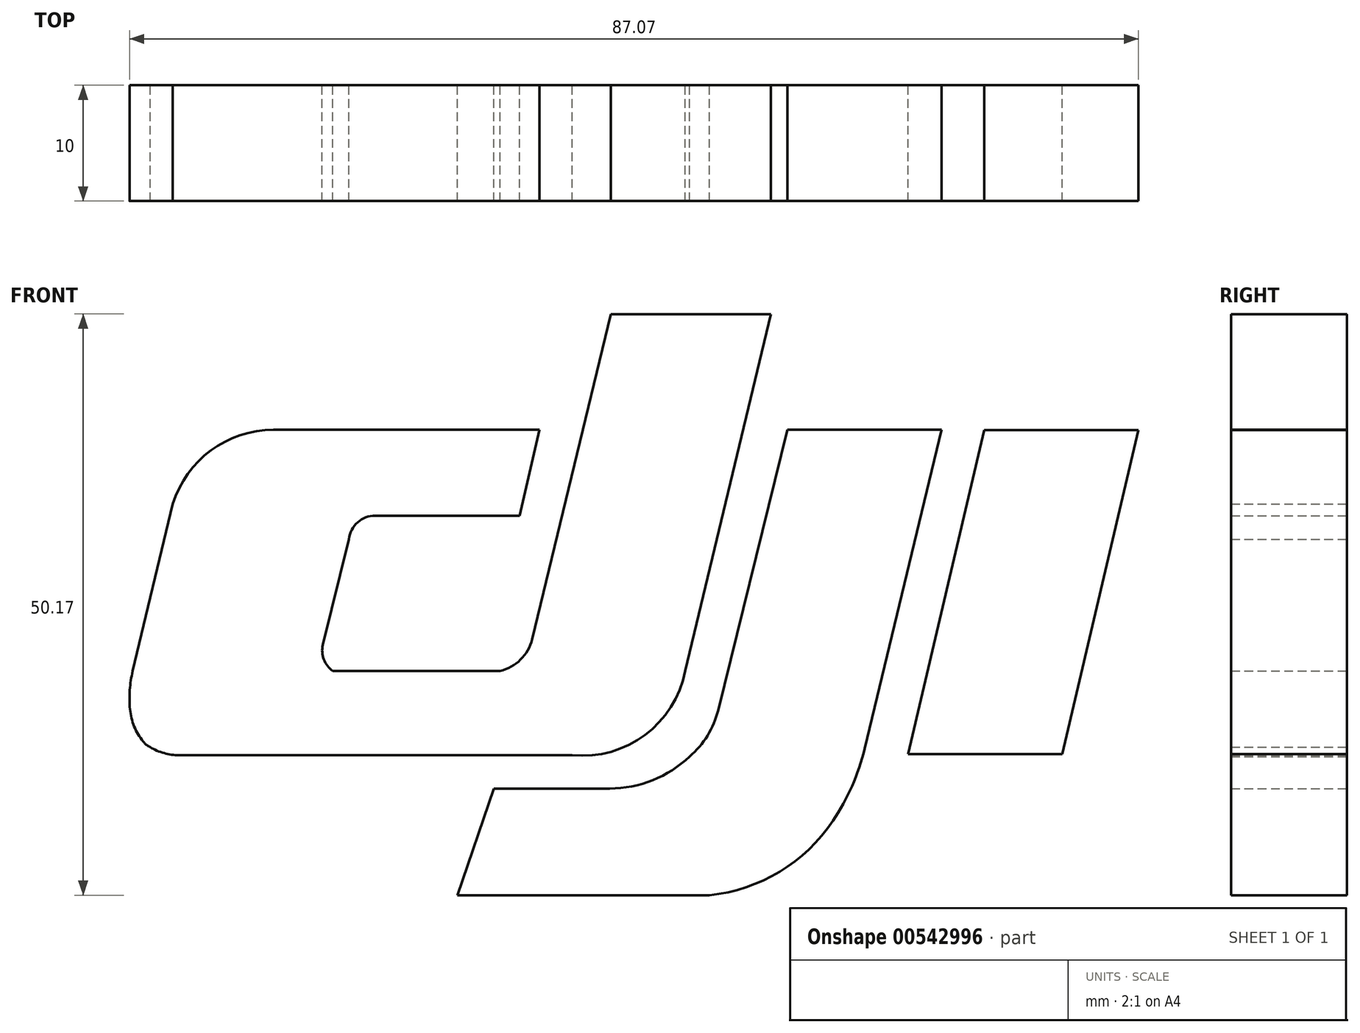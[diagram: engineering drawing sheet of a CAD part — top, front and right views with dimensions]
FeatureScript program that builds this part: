
annotation { "Feature Type Name" : "Feature", "Feature Type Description" : "" }
export const myFeature = defineFeature(function(context is Context, id is Id, definition is map)
    precondition{}
    {
        {
            var Q0;
            Q0=qCreatedBy(makeId("Front.planeOp"),FACE);
            var sketch = newSketch(context, id + "F0", { "sketchPlane" : qUnion([Q0])});
            skLineSegment(sketch, "E0", {"start": v(11.76, 25.1) * mm, "end": v(-2.04, 25.1) * mm});
            skLineSegment(sketch, "E1", {"start": v(-2.04, 25.1) * mm, "end": v(-8.84, -2.97) * mm});
            skLineSegment(sketch, "E2", {"start": v(11.76, 25.1) * mm, "end": v(4.38, -5.7) * mm});
            skLineSegment(sketch, "E3", {"start": v(-8.2, 15.11) * mm, "end": v(-9.92, 7.7) * mm});
            skLineSegment(sketch, "E4", {"start": v(-9.92, 7.7) * mm, "end": v(-22.36, 7.7) * mm});
            skLineSegment(sketch, "E5", {"start": v(-8.2, 15.11) * mm, "end": v(-31.15, 15.11) * mm});
            skLineSegment(sketch, "E6", {"start": v(-39.84, 8.7) * mm, "end": v(-43.3, -5.71) * mm});
            skLineSegment(sketch, "E7", {"start": v(-39.3, -12.98) * mm, "end": v(-5.37, -12.98) * mm});
            skArc(sketch, "E8", {"start": v(-31.15, 15.11) * mm, "mid": v(-36.55, 13.33) * mm, "end": v(-39.84, 8.7) * mm});
            skArc(sketch, "E9", {"start": v(-8.84, -2.97) * mm, "mid": v(-9.83, -4.73) * mm, "end": v(-11.6, -5.7) * mm});
            skArc(sketch, "E10", {"start": v(-22.36, 7.7) * mm, "mid": v(-23.89, 7.13) * mm, "end": v(-24.64, 5.68) * mm});
            skLineSegment(sketch, "E11", {"start": v(-24.64, 5.68) * mm, "end": v(-26.89, -3.45) * mm});
            skArc(sketch, "E12", {"start": v(-26.89, -3.45) * mm, "mid": v(-26.8, -4.71) * mm, "end": v(-26.03, -5.7) * mm});
            skLineSegment(sketch, "E13", {"start": v(-26.03, -5.7) * mm, "end": v(-11.6, -5.7) * mm});
            skArc(sketch, "E14", {"start": v(-43.3, -5.71) * mm, "mid": v(-43.55, -7.36) * mm, "end": v(-43.54, -9.02) * mm});
            skArc(sketch, "E15", {"start": v(-43.54, -9.02) * mm, "mid": v(-43.17, -10.5) * mm, "end": v(-42.4, -11.8) * mm});
            skArc(sketch, "E16", {"start": v(-42.4, -11.8) * mm, "mid": v(-42.12, -12.07) * mm, "end": v(-41.8, -12.28) * mm});
            skArc(sketch, "E17", {"start": v(-39.3, -12.98) * mm, "mid": v(-40.6, -12.8) * mm, "end": v(-41.8, -12.28) * mm});
            skArc(sketch, "E18", {"start": v(-5.37, -12.98) * mm, "mid": v(0.91, -11.23) * mm, "end": v(4.38, -5.7) * mm});
            skSolve(sketch);
        }
        {
            var Q0;
            Q0=qCreatedBy(makeId("Front.planeOp"),FACE);
            var sketch = newSketch(context, id + "F1", { "sketchPlane" : qUnion([Q0])});
            skLineSegment(sketch, "E19", {"start": v(26.5, 15.12) * mm, "end": v(13.2, 15.12) * mm});
            skLineSegment(sketch, "E20", {"start": v(26.5, 15.12) * mm, "end": v(19.86, -12.42) * mm});
            skLineSegment(sketch, "E21", {"start": v(13.2, 15.12) * mm, "end": v(7.22, -9.1) * mm});
            skArc(sketch, "E22", {"start": v(17.13, -18.64) * mm, "mid": v(18.78, -15.65) * mm, "end": v(19.86, -12.42) * mm});
            skArc(sketch, "E23", {"start": v(6.48, -25.06) * mm, "mid": v(12.53, -23.04) * mm, "end": v(17.13, -18.64) * mm});
            skLineSegment(sketch, "E24", {"start": v(6.48, -25.06) * mm, "end": v(-15.28, -25.06) * mm});
            skLineSegment(sketch, "E25", {"start": v(-15.28, -25.06) * mm, "end": v(-12.12, -15.85) * mm});
            skLineSegment(sketch, "E26", {"start": v(-12.12, -15.85) * mm, "end": v(-2.14, -15.85) * mm});
            skArc(sketch, "E27", {"start": v(4.75, -13.1) * mm, "mid": v(6.3, -11.28) * mm, "end": v(7.22, -9.1) * mm});
            skArc(sketch, "E28", {"start": v(-2.14, -15.85) * mm, "mid": v(1.57, -15.13) * mm, "end": v(4.75, -13.1) * mm});
            skSolve(sketch);
        }
        {
            var Q0;
            Q0=qCreatedBy(makeId("Front.planeOp"),FACE);
            var sketch = newSketch(context, id + "F2", { "sketchPlane" : qUnion([Q0])});
            skLineSegment(sketch, "E29", {"start": v(43.49, 15.08) * mm, "end": v(30.18, 15.08) * mm});
            skLineSegment(sketch, "E30", {"start": v(30.18, 15.08) * mm, "end": v(23.6, -12.88) * mm});
            skLineSegment(sketch, "E31", {"start": v(23.6, -12.88) * mm, "end": v(36.92, -12.88) * mm});
            skLineSegment(sketch, "E32", {"start": v(36.92, -12.88) * mm, "end": v(43.49, 15.08) * mm});
            skSolve(sketch);
        }
        {
            var Q0;
            Q0=makeQuery(id+"F0.imprint","IMPRINT",FACE,{"disambiguationData":[TD([[makeQuery(id+"F0.imprint","IMPRINT",EDGE,{"derivedFrom":sQuery(id+"F0.wireOp",EDGE,"E0")}),1.0]])]});
            var Q1;
            Q1=makeQuery(id+"F1.imprint","IMPRINT",FACE,{"disambiguationData":[TD([[makeQuery(id+"F1.imprint","IMPRINT",EDGE,{"derivedFrom":sQuery(id+"F1.wireOp",EDGE,"E19")}),1.0]])]});
            var Q2;
            Q2=makeQuery(id+"F2.imprint","IMPRINT",FACE,{"disambiguationData":[TD([[makeQuery(id+"F2.imprint","IMPRINT",EDGE,{"derivedFrom":sQuery(id+"F2.wireOp",EDGE,"E29")}),1.0]])]});
            extrude(context, id + "F3", {"entities" : qUnion([Q0, Q1, Q2]), "depth" : 10 * mm, "offsetDistance" : 25 * mm});
        }
    });
